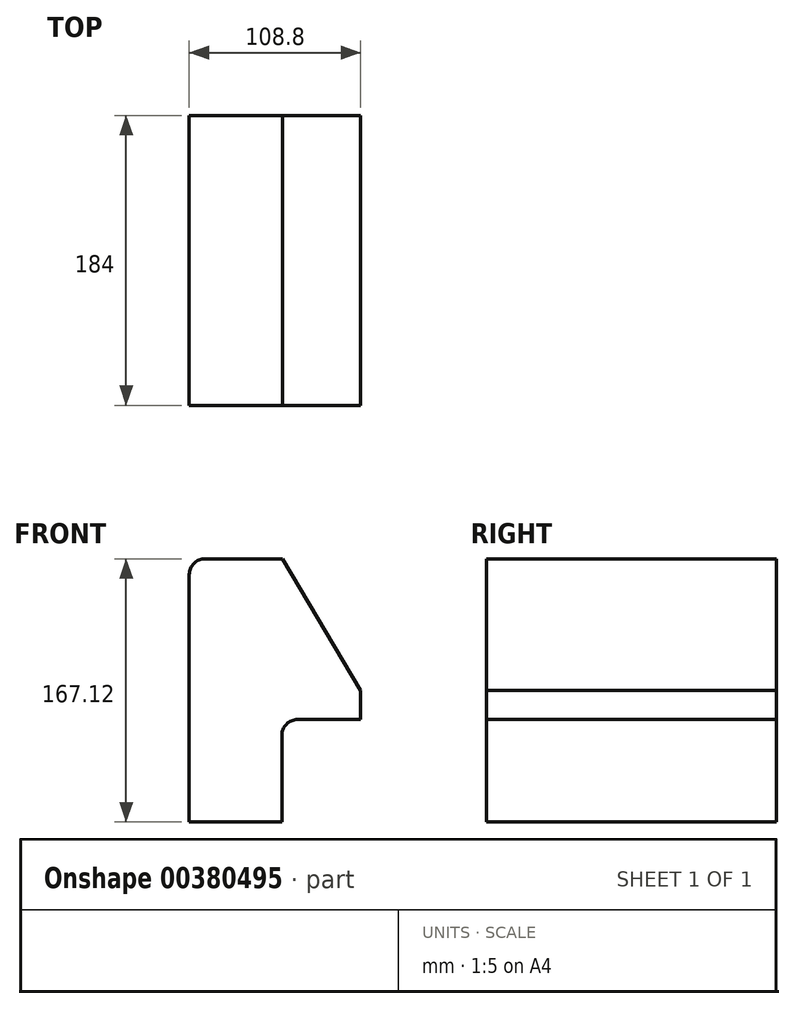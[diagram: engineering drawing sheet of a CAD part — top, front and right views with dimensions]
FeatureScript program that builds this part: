
annotation { "Feature Type Name" : "Feature", "Feature Type Description" : "" }
export const myFeature = defineFeature(function(context is Context, id is Id, definition is map)
    precondition{}
    {
        {
            var Q0;
            Q0=qCreatedBy(makeId("Front.planeOp"),FACE);
            var sketch = newSketch(context, id + "F0", { "sketchPlane" : qUnion([Q0])});
            skLineSegment(sketch, "E0.bottom", {"start": v(0, 0) * mm, "end": v(108.8, 0) * mm});
            skLineSegment(sketch, "E0.top", {"start": v(10, 167.12) * mm, "end": v(59.4, 167.12) * mm});
            skLineSegment(sketch, "E0.left", {"start": v(0, 0) * mm, "end": v(0, 157.12) * mm});
            skLineSegment(sketch, "E0.right", {"start": v(108.8, 0) * mm, "end": v(108.8, 83.56) * mm});
            skPoint(sketch, "E1.visualSharp", {"position": v(0, 167.12) * mm});
            skArc(sketch, "E1.filletArc", {"start": v(10, 167.12) * mm, "mid": v(2.93, 164.2) * mm, "end": v(0, 157.12) * mm});
            skLineSegment(sketch, "E2", {"start": v(59.4, 167.12) * mm, "end": v(108.8, 83.56) * mm});
            skPoint(sketch, "E3.orphan", {"position": v(108.8, 167.12) * mm});
            skSolve(sketch);
        }
        {
            var Q0;
            Q0=makeQuery(id+"F0.imprint","IMPRINT",FACE,{"disambiguationData":[TD([[makeQuery(id+"F0.imprint","IMPRINT",EDGE,{"derivedFrom":sQuery(id+"F0.wireOp",EDGE,"E0.bottom")}),1.0]])]});
            extrude(context, id + "F1", {"entities" : qUnion([Q0]), "depth" : 184 * mm, "offsetDistance" : 25 * mm});
        }
        {
            var Q0;
            Q0=makeQuery(id+"F1.opExtrude","CAP_FACE",FACE,{"disambiguationData":[OSD([sQuery(id+"F0.wireOp",EDGE,"E0.bottom"),sQuery(id+"F0.wireOp",EDGE,"E0.top"),sQuery(id+"F0.wireOp",EDGE,"E0.left"),sQuery(id+"F0.wireOp",EDGE,"E0.right"),sQuery(id+"F0.wireOp",EDGE,"E1.filletArc"),sQuery(id+"F0.wireOp",EDGE,"E2")])],"isStart":false});
            var sketch = newSketch(context, id + "F2", { "sketchPlane" : qUnion([Q0])});
            skLineSegment(sketch, "E4.bottom", {"start": v(108.8, 0) * mm, "end": v(58.8, 0) * mm});
            skLineSegment(sketch, "E4.top", {"start": v(108.8, 65) * mm, "end": v(58.8, 65) * mm});
            skLineSegment(sketch, "E4.left", {"start": v(108.8, 0) * mm, "end": v(108.8, 65) * mm});
            skLineSegment(sketch, "E4.right", {"start": v(58.8, 0) * mm, "end": v(58.8, 65) * mm});
            skPoint(sketch, "E4.middle", {"position": v(83.8, 32.5) * mm});
            skSolve(sketch);
        }
        {
            var Q0;
            Q0 = qSketchRegion(id + "F2", true);
            extrude(context, id + "F3", {"entities" : qUnion([Q0]), "operationType" : NewBodyOperationType.REMOVE, "oppositeDirection" : true, "depth" : 321 * mm, "offsetDistance" : 25 * mm});
        }
        {
            var Q0;
            Q0=makeQuery(id+"F3.boolean.opBoolean","COPY",EDGE,{"derivedFrom":makeQuery(id+"F3.opExtrude","SWEPT_EDGE",EDGE,{"disambiguationData":[OSD([sQuery(id+"F2.wireOp",EDGE,"E4.top"),sQuery(id+"F2.wireOp",EDGE,"E4.right")])]})});
            fillet(context, id + "F4", {"entities" : qUnion([Q0]), "radius" : 10 * mm, "tangentPropagation" : true, "allowEdgeOverflow" : false});
        }
    });
